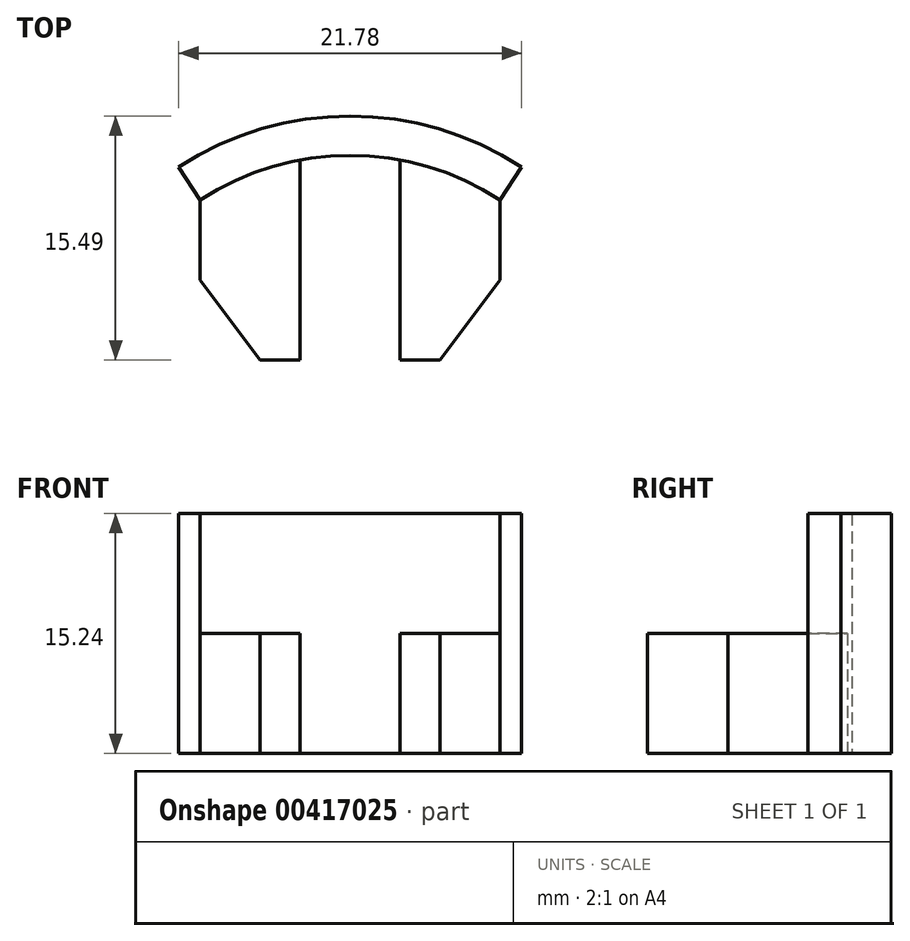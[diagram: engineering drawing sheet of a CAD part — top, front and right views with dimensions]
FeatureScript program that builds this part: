
annotation { "Feature Type Name" : "Feature", "Feature Type Description" : "" }
export const myFeature = defineFeature(function(context is Context, id is Id, definition is map)
    precondition{}
    {
        {
            var Q0;
            Q0=qCreatedBy(makeId("Top.planeOp"),FACE);
            var sketch = newSketch(context, id + "F0", { "sketchPlane" : qUnion([Q0])});
            skCircle(sketch, "E0", {"center": v(0, 0) * mm, "radius": 17.5 * mm});
            skCircle(sketch, "E1", {"center": v(0, 0) * mm, "radius": 20 * mm});
            skPoint(sketch, "E2", {"position": v(3.17, 17.2) * mm});
            skPoint(sketch, "E3", {"position": v(-3.17, 17.2) * mm});
            skPoint(sketch, "E4", {"position": v(9.53, 14.68) * mm});
            skPoint(sketch, "E5", {"position": v(-9.53, 14.68) * mm});
            skLineSegment(sketch, "E6.bottom", {"start": v(-3.17, 17.2) * mm, "end": v(3.17, 17.2) * mm});
            skLineSegment(sketch, "E6.top", {"start": v(-3.17, 4.5) * mm, "end": v(3.17, 4.5) * mm});
            skLineSegment(sketch, "E6.left", {"start": v(-3.17, 17.2) * mm, "end": v(-3.17, 4.5) * mm});
            skLineSegment(sketch, "E6.right", {"start": v(3.17, 17.2) * mm, "end": v(3.18, 4.5) * mm});
            skLineSegment(sketch, "E7.bottom", {"start": v(3.17, 17.2) * mm, "end": v(9.52, 17.2) * mm});
            skLineSegment(sketch, "E7.top", {"start": v(3.18, 4.5) * mm, "end": v(9.52, 4.5) * mm});
            skLineSegment(sketch, "E7.left", {"start": v(3.17, 17.2) * mm, "end": v(3.17, 4.5) * mm});
            skLineSegment(sketch, "E7.right", {"start": v(9.52, 17.2) * mm, "end": v(9.52, 4.5) * mm});
            skLineSegment(sketch, "E8.bottom", {"start": v(-3.17, 17.2) * mm, "end": v(-9.53, 17.2) * mm});
            skLineSegment(sketch, "E8.top", {"start": v(-3.17, 4.5) * mm, "end": v(-9.52, 4.5) * mm});
            skLineSegment(sketch, "E8.right", {"start": v(-9.53, 17.2) * mm, "end": v(-9.53, 4.5) * mm});
            skLineSegment(sketch, "E9.bottom", {"start": v(-9.52, 4.5) * mm, "end": v(9.52, 4.5) * mm});
            skLineSegment(sketch, "E9.top", {"start": v(-9.52, 32.58) * mm, "end": v(9.52, 32.58) * mm});
            skLineSegment(sketch, "E9.left", {"start": v(-9.52, 4.5) * mm, "end": v(-9.52, 32.58) * mm});
            skLineSegment(sketch, "E9.right", {"start": v(9.52, 4.5) * mm, "end": v(9.52, 32.58) * mm});
            skPoint(sketch, "E10", {"position": v(-9.53, 9.6) * mm});
            skPoint(sketch, "E11", {"position": v(9.52, 9.6) * mm});
            skLineSegment(sketch, "E12", {"start": v(-3.17, 4.5) * mm, "end": v(-5.71, 4.5) * mm});
            skLineSegment(sketch, "E13", {"start": v(-5.71, 4.5) * mm, "end": v(-3.17, 4.5) * mm});
            skLineSegment(sketch, "E14", {"start": v(-9.53, 9.6) * mm, "end": v(-5.71, 4.5) * mm});
            skLineSegment(sketch, "E15", {"start": v(3.17, 4.5) * mm, "end": v(5.71, 4.5) * mm});
            skLineSegment(sketch, "E16", {"start": v(5.71, 4.5) * mm, "end": v(3.18, 4.5) * mm});
            skLineSegment(sketch, "E17", {"start": v(5.71, 4.5) * mm, "end": v(9.52, 9.6) * mm});
            skLineSegment(sketch, "E18", {"start": v(-9.53, 14.68) * mm, "end": v(-10.89, 16.78) * mm});
            skLineSegment(sketch, "E19", {"start": v(-9.53, 14.68) * mm, "end": v(-13.63, 12.02) * mm});
            skLineSegment(sketch, "E20", {"start": v(-13.63, 12.02) * mm, "end": v(-9.53, 14.68) * mm});
            skLineSegment(sketch, "E21", {"start": v(9.53, 14.68) * mm, "end": v(10.89, 16.78) * mm});
            skLineSegment(sketch, "E22", {"start": v(9.53, 14.68) * mm, "end": v(12.15, 12.98) * mm});
            skSolve(sketch);
        }
        {
            var Q0;
            {var subQ4=sQuery(id+"F0.wireOp",EDGE,"E6.left");Q0=makeQuery(id+"F0.imprint","IMPRINT",FACE,{"disambiguationData":[TD([[makeQuery(id+"F0.imprint","IMPRINT",EDGE,{"derivedFrom":subQ4}),-1.0]])]});}
            var Q1;
            {var subQ4=sQuery(id+"F0.wireOp",EDGE,"E7.left");Q1=makeQuery(id+"F0.imprint","IMPRINT",FACE,{"disambiguationData":[TD([[makeQuery(id+"F0.imprint","IMPRINT",EDGE,{"derivedFrom":subQ4}),1.0]])]});}
            extrude(context, id + "F1", {"entities" : qUnion([Q0, Q1]), "depth" : 7.62 * mm});
        }
        {
            var Q0;
            {var subQ0=sQuery(id+"F0.wireOp",EDGE,"E8.bottom");Q0=makeQuery(id+"F0.imprint","IMPRINT",FACE,{"disambiguationData":[TD([[makeQuery(id+"F0.imprint","IMPRINT",EDGE,{"derivedFrom":subQ0}),1.0]])]});}
            var Q1;
            {var subQ0=sQuery(id+"F0.wireOp",EDGE,"E7.bottom");Q1=makeQuery(id+"F0.imprint","IMPRINT",FACE,{"disambiguationData":[TD([[makeQuery(id+"F0.imprint","IMPRINT",EDGE,{"derivedFrom":subQ0}),1.0]])]});}
            var Q2;
            {var subQ0=sQuery(id+"F0.wireOp",EDGE,"E7.bottom");Q2=makeQuery(id+"F0.imprint","IMPRINT",FACE,{"disambiguationData":[TD([[makeQuery(id+"F0.imprint","IMPRINT",EDGE,{"derivedFrom":subQ0}),-1.0]])]});}
            var Q3;
            {var subQ0=sQuery(id+"F0.wireOp",EDGE,"E18");Q3=makeQuery(id+"F0.imprint","IMPRINT",FACE,{"disambiguationData":[TD([[makeQuery(id+"F0.imprint","IMPRINT",EDGE,{"derivedFrom":subQ0}),-1.0]])]});}
            var Q4;
            {var subQ0=sQuery(id+"F0.wireOp",EDGE,"E21");Q4=makeQuery(id+"F0.imprint","IMPRINT",FACE,{"disambiguationData":[TD([[makeQuery(id+"F0.imprint","IMPRINT",EDGE,{"derivedFrom":subQ0}),1.0]])]});}
            extrude(context, id + "F2", {"entities" : qUnion([Q0, Q1, Q2, Q3, Q4]), "depth" : 15.24 * mm});
        }
    });
